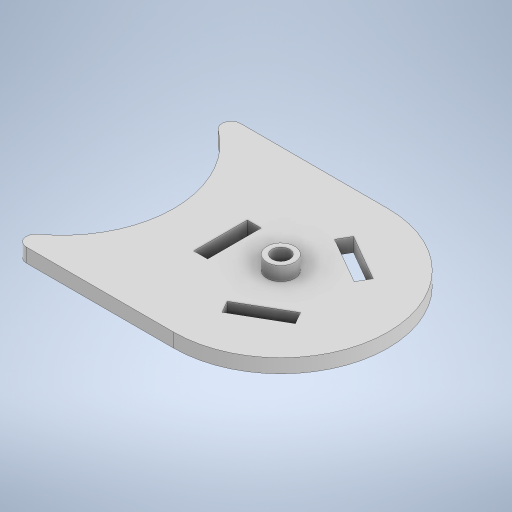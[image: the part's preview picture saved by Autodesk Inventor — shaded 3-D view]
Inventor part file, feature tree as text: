
AUTODESK INVENTOR PART (.ipt)
format: ipt  version: 2024.1 (Build 281209000, 209)  size: 285,184 bytes
history: native  units: mm
features: extrude x6, sketch x6, other x1, fillet x1
ambient origin geometry x8: Origin, YZ Plane, XZ Plane, XY Plane, X Axis, Y Axis, Z Axis, Center Point
bodies: Body1 (feature_tree)
feature tree (14):
  other  "ソリッド1"
  extrude  "押し出し1"  Depth=12.0mm
  extrude  "押し出し2"  Depth=1.0mm TaperAngle=0.0deg
  extrude  "押し出し3"  Depth=6.0mm
  extrude  "押し出し4"  Depth=3.0mm TaperAngle=0.0deg
  extrude  "押し出し5"  Depth=3.8mm
  fillet  "フィレット1"  [1 undecoded]
  extrude  "押し出し6"  Depth=47.1mm
  sketch  "スケッチ1"
  sketch  "スケッチ2"
  sketch  "スケッチ3"
  sketch  "スケッチ4"
  sketch  "スケッチ5"
  sketch  "スケッチ6"
note: 1 required parameter value undecoded (feature->parameter linkage not recoverable at this tier; creation-order binding heuristic only, values carry confidence <= 0.55)
